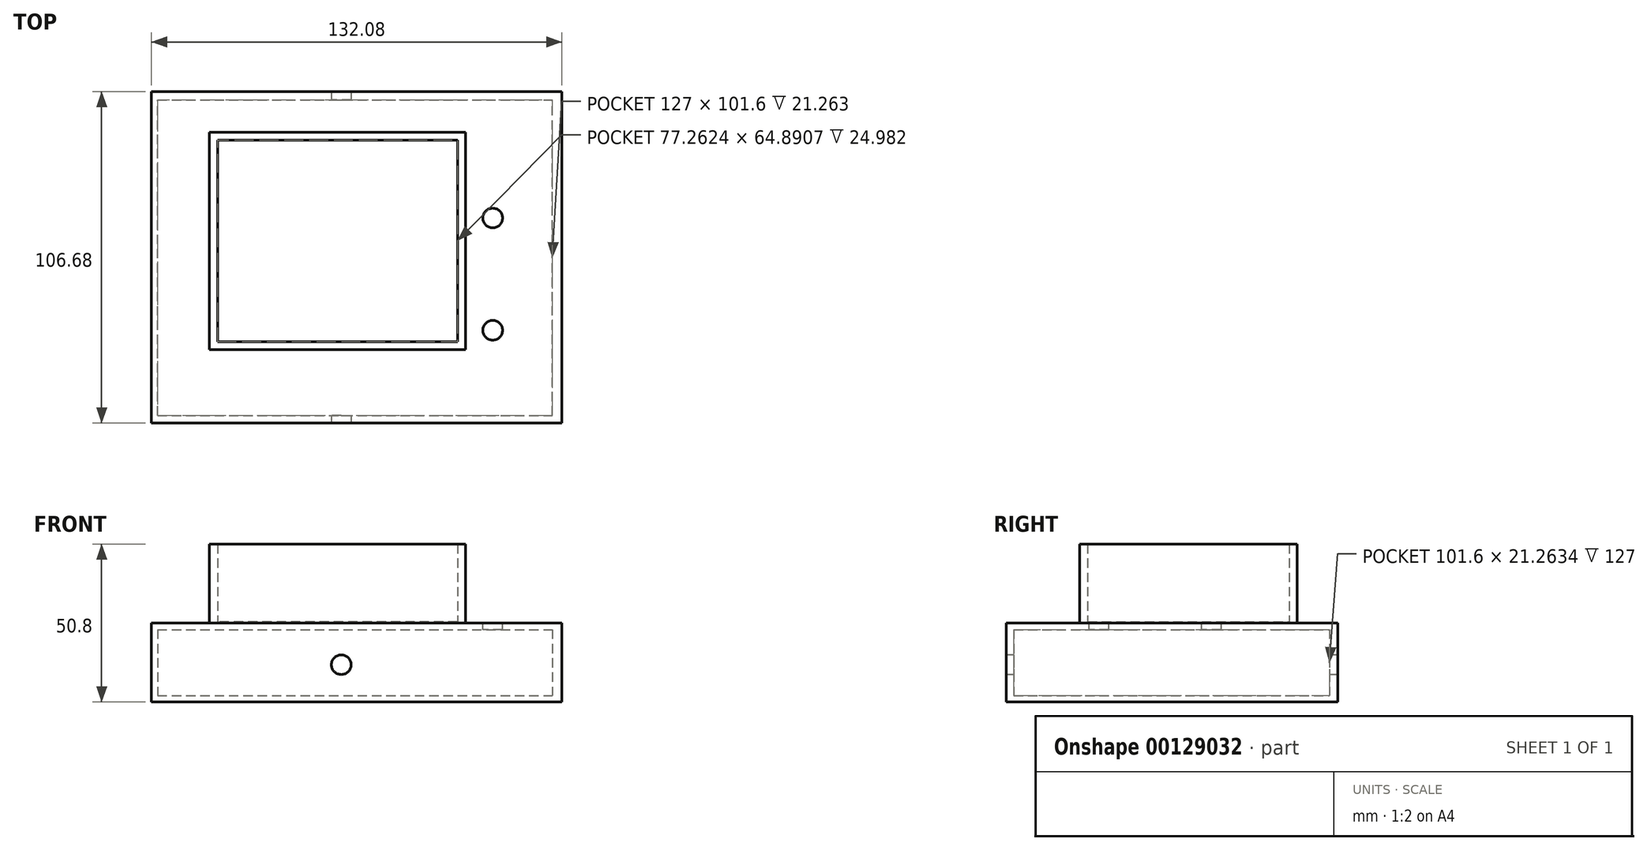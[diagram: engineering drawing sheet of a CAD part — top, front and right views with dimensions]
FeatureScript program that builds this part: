
annotation { "Feature Type Name" : "Feature", "Feature Type Description" : "" }
export const myFeature = defineFeature(function(context is Context, id is Id, definition is map)
    precondition{}
    {
        {
            var Q0;
            Q0=qCreatedBy(makeId("Top.planeOp"),FACE);
            var sketch = newSketch(context, id + "F0", { "sketchPlane" : qUnion([Q0])});
            skLineSegment(sketch, "E0.bottom", {"start": v(-59.12, 50.27) * mm, "end": v(67.88, 50.27) * mm});
            skLineSegment(sketch, "E0.top", {"start": v(-59.12, -51.33) * mm, "end": v(67.88, -51.33) * mm});
            skLineSegment(sketch, "E0.left", {"start": v(-59.12, 50.27) * mm, "end": v(-59.12, -51.33) * mm});
            skLineSegment(sketch, "E0.right", {"start": v(67.88, 50.27) * mm, "end": v(67.88, -51.33) * mm});
            skLineSegment(sketch, "E1.bottom", {"start": v(-61.08, 52.93) * mm, "end": v(71, 52.93) * mm});
            skLineSegment(sketch, "E1.top", {"start": v(-61.08, -53.75) * mm, "end": v(71, -53.75) * mm});
            skLineSegment(sketch, "E1.left", {"start": v(-61.08, 52.93) * mm, "end": v(-61.08, -53.75) * mm});
            skLineSegment(sketch, "E1.right", {"start": v(71, 52.93) * mm, "end": v(71, -53.75) * mm});
            skSolve(sketch);
        }
        {
            var Q0;
            Q0=makeQuery(id+"F0.imprint","IMPRINT",FACE,{"disambiguationData":[TD([[makeQuery(id+"F0.imprint","IMPRINT",EDGE,{"derivedFrom":sQuery(id+"F0.wireOp",EDGE,"E0.bottom")}),1.0]])]});
            extrude(context, id + "F1", {"entities" : qUnion([Q0]), "depth" : 25.4 * mm});
        }
        {
            var Q0;
            Q0=makeQuery(id+"F1.opExtrude","SWEPT_FACE",FACE,{"disambiguationData":[OSD([sQuery(id+"F0.wireOp",EDGE,"E0.bottom")])]});
            var sketch = newSketch(context, id + "F2", { "sketchPlane" : qUnion([Q0])});
            skLineSegment(sketch, "E2.bottom", {"start": v(-59.12, 25.4) * mm, "end": v(67.88, 25.4) * mm});
            skLineSegment(sketch, "E2.top", {"start": v(-59.12, 23.28) * mm, "end": v(67.88, 23.28) * mm});
            skLineSegment(sketch, "E2.left", {"start": v(-59.12, 25.4) * mm, "end": v(-59.12, 23.28) * mm});
            skLineSegment(sketch, "E2.right", {"start": v(67.88, 25.4) * mm, "end": v(67.88, 23.28) * mm});
            skLineSegment(sketch, "E3.bottom", {"start": v(-59.12, 0) * mm, "end": v(67.88, 0) * mm});
            skLineSegment(sketch, "E3.top", {"start": v(-59.12, 2.01) * mm, "end": v(67.88, 2.01) * mm});
            skLineSegment(sketch, "E3.left", {"start": v(-59.12, 0) * mm, "end": v(-59.12, 2.01) * mm});
            skLineSegment(sketch, "E3.right", {"start": v(67.88, 0) * mm, "end": v(67.88, 2.01) * mm});
            skSolve(sketch);
        }
        {
            var Q0;
            Q0=makeQuery(id+"F2.imprint","IMPRINT",FACE,{"disambiguationData":[TD([[makeQuery(id+"F2.imprint","IMPRINT",EDGE,{"derivedFrom":sQuery(id+"F2.wireOp",EDGE,"E3.bottom")}),1.0]])]});
            extrude(context, id + "F3", {"entities" : qUnion([Q0]), "operationType" : NewBodyOperationType.ADD, "depth" : 101.6 * mm});
        }
        {
            var Q0;
            Q0=makeQuery(id+"F1.opExtrude","SWEPT_FACE",FACE,{"disambiguationData":[OSD([sQuery(id+"F0.wireOp",EDGE,"E1.top")])]});
            var sketch = newSketch(context, id + "F4", { "sketchPlane" : qUnion([Q0])});
            skCircle(sketch, "E4", {"center": v(0, 12) * mm, "radius": 4.13 * mm});
            skSolve(sketch);
        }
        {
            var Q0;
            Q0=sQuery(id+"F4.wireOp",VERTEX,"E4.center");
            var Q1;
            Q1=makeQuery(id+"F1.opExtrude","SWEPT_BODY",BODY,{"disambiguationData":[OSD([sQuery(id+"F0.wireOp",EDGE,"E0.bottom"),sQuery(id+"F0.wireOp",EDGE,"E0.top"),sQuery(id+"F0.wireOp",EDGE,"E0.left"),sQuery(id+"F0.wireOp",EDGE,"E0.right"),sQuery(id+"F0.wireOp",EDGE,"E1.bottom"),sQuery(id+"F0.wireOp",EDGE,"E1.top"),sQuery(id+"F0.wireOp",EDGE,"E1.left"),sQuery(id+"F0.wireOp",EDGE,"E1.right")])]});
            hole(context, id + "F5", {"style" : HoleStyle.SIMPLE, "endStyle" : HoleEndStyle.THROUGH, "holeDiameter" : 6.35 * mm, "locations" : qUnion([Q0]), "scope" : qUnion([Q1]), "isTappedThrough" : true});
        }
        {
            var Q0;
            Q0 = qSketchRegion(id + "F2", true);
            extrude(context, id + "F6", {"entities" : qUnion([Q0]), "operationType" : NewBodyOperationType.ADD, "depth" : 101.6 * mm});
        }
        {
            var Q0;
            Q0=makeQuery(id+"F6.boolean.opBoolean","MERGE",FACE,{"derivedFrom":[makeQuery(id+"F1.opExtrude","CAP_FACE",FACE,{"disambiguationData":[OSD([sQuery(id+"F0.wireOp",EDGE,"E0.bottom"),sQuery(id+"F0.wireOp",EDGE,"E0.top"),sQuery(id+"F0.wireOp",EDGE,"E0.left"),sQuery(id+"F0.wireOp",EDGE,"E0.right"),sQuery(id+"F0.wireOp",EDGE,"E1.bottom"),sQuery(id+"F0.wireOp",EDGE,"E1.top"),sQuery(id+"F0.wireOp",EDGE,"E1.left"),sQuery(id+"F0.wireOp",EDGE,"E1.right")])],"isStart":false}),makeQuery(id+"F6.opExtrude","SWEPT_FACE",FACE,{"disambiguationData":[OSD([sQuery(id+"F2.wireOp",EDGE,"E2.bottom")])]})]});
            var sketch = newSketch(context, id + "F7", { "sketchPlane" : qUnion([Q0])});
            skLineSegment(sketch, "E5.bottom", {"start": v(-39.82, 36.92) * mm, "end": v(36.38, 36.92) * mm});
            skLineSegment(sketch, "E5.top", {"start": v(-39.82, -26.58) * mm, "end": v(36.38, -26.58) * mm});
            skLineSegment(sketch, "E5.left", {"start": v(-39.82, 36.92) * mm, "end": v(-39.82, -26.58) * mm});
            skLineSegment(sketch, "E5.right", {"start": v(36.38, 36.92) * mm, "end": v(36.38, -26.58) * mm});
            skLineSegment(sketch, "E6.bottom", {"start": v(-42.39, 39.85) * mm, "end": v(39.95, 39.85) * mm});
            skLineSegment(sketch, "E6.top", {"start": v(-42.39, -30.12) * mm, "end": v(39.95, -30.12) * mm});
            skLineSegment(sketch, "E6.left", {"start": v(-42.39, 39.85) * mm, "end": v(-42.39, -30.12) * mm});
            skLineSegment(sketch, "E6.right", {"start": v(39.95, 39.85) * mm, "end": v(39.95, -30.12) * mm});
            skSolve(sketch);
        }
        {
            var Q0;
            Q0=makeQuery(id+"F7.imprint","IMPRINT",FACE,{"disambiguationData":[TD([[makeQuery(id+"F7.imprint","IMPRINT",EDGE,{"derivedFrom":sQuery(id+"F7.wireOp",EDGE,"E5.bottom")}),1.0]])]});
            var Q1;
            Q1=makeQuery(id+"F7.imprint","IMPRINT",FACE,{"disambiguationData":[TD([[makeQuery(id+"F7.imprint","IMPRINT",EDGE,{"derivedFrom":sQuery(id+"F7.wireOp",EDGE,"E5.bottom")}),-1.0]])]});
            extrude(context, id + "F8", {"entities" : qUnion([Q0, Q1]), "operationType" : NewBodyOperationType.ADD, "depth" : 25.4 * mm});
        }
        {
            var Q0;
            Q0=makeQuery(id+"F6.boolean.opBoolean","MERGE",FACE,{"derivedFrom":[makeQuery(id+"F1.opExtrude","CAP_FACE",FACE,{"disambiguationData":[OSD([sQuery(id+"F0.wireOp",EDGE,"E0.bottom"),sQuery(id+"F0.wireOp",EDGE,"E0.top"),sQuery(id+"F0.wireOp",EDGE,"E0.left"),sQuery(id+"F0.wireOp",EDGE,"E0.right"),sQuery(id+"F0.wireOp",EDGE,"E1.bottom"),sQuery(id+"F0.wireOp",EDGE,"E1.top"),sQuery(id+"F0.wireOp",EDGE,"E1.left"),sQuery(id+"F0.wireOp",EDGE,"E1.right")])],"isStart":false}),makeQuery(id+"F6.opExtrude","SWEPT_FACE",FACE,{"disambiguationData":[OSD([sQuery(id+"F2.wireOp",EDGE,"E2.bottom")])]})]});
            var sketch = newSketch(context, id + "F9", { "sketchPlane" : qUnion([Q0])});
            skLineSegment(sketch, "E7.bottom", {"start": v(48.73, -23.9) * mm, "end": v(59.16, -23.9) * mm});
            skLineSegment(sketch, "E7.top", {"start": v(48.73, 12.23) * mm, "end": v(59.16, 12.23) * mm});
            skLineSegment(sketch, "E7.left", {"start": v(48.73, -23.9) * mm, "end": v(48.73, 12.23) * mm});
            skLineSegment(sketch, "E7.right", {"start": v(59.16, -23.9) * mm, "end": v(59.16, 12.23) * mm});
            skSolve(sketch);
        }
        {
            var Q0;
            Q0=sQuery(id+"F9.wireOp",VERTEX,"E7.bottom.start");
            var Q1;
            Q1=sQuery(id+"F9.wireOp",VERTEX,"E7.top.start");
            var Q2;
            Q2=makeQuery(id+"F1.opExtrude","SWEPT_BODY",BODY,{"disambiguationData":[OSD([sQuery(id+"F0.wireOp",EDGE,"E0.bottom"),sQuery(id+"F0.wireOp",EDGE,"E0.top"),sQuery(id+"F0.wireOp",EDGE,"E0.left"),sQuery(id+"F0.wireOp",EDGE,"E0.right"),sQuery(id+"F0.wireOp",EDGE,"E1.bottom"),sQuery(id+"F0.wireOp",EDGE,"E1.top"),sQuery(id+"F0.wireOp",EDGE,"E1.left"),sQuery(id+"F0.wireOp",EDGE,"E1.right")])]});
            hole(context, id + "F10", {"style" : HoleStyle.SIMPLE, "endStyle" : HoleEndStyle.BLIND, "holeDiameter" : 6.35 * mm, "holeDepth" : 12.7 * mm, "locations" : qUnion([Q0, Q1]), "scope" : qUnion([Q2])});
        }
        {
            var Q0;
            Q0=makeQuery(id+"F8.opExtrude","CAP_FACE",FACE,{"disambiguationData":[OSD([sQuery(id+"F7.wireOp",EDGE,"E6.bottom"),sQuery(id+"F7.wireOp",EDGE,"E6.top"),sQuery(id+"F7.wireOp",EDGE,"E6.left"),sQuery(id+"F7.wireOp",EDGE,"E6.right")])],"isStart":false});
            shell(context, id + "F11", {"entities" : qUnion([Q0]), "thickness" : 2.54 * mm});
        }
    });
